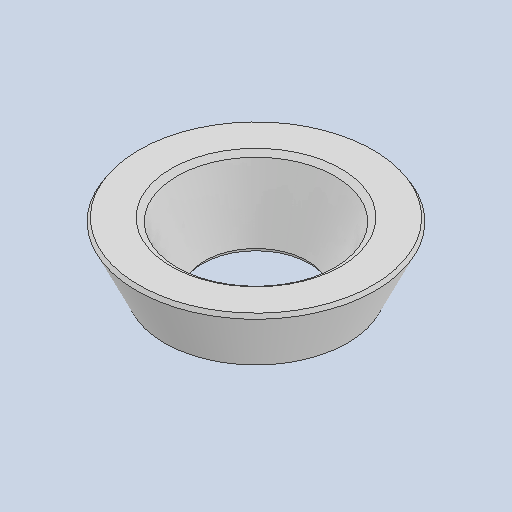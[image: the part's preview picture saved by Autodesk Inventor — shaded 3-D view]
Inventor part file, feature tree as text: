
AUTODESK INVENTOR PART (.ipt)
format: ipt  version: 2023 (Build 270158000, 158)  size: 247,808 bytes
history: native  units: mm
features: revolve x1, chamfer x1, sketch x1
ambient origin geometry x8: Origin, YZ Plane, XZ Plane, XY Plane, X Axis, Y Axis, Z Axis, Center Point
bodies: Solid1 (feature_tree)
feature tree (3):
  revolve  "Revolution1"  [1 undecoded]
  chamfer  "Chamfer1"  Distance=8.0mm
  sketch  "Sketch1"  dims[d1=3.3mm d3=2.0mm d5=8.0mm d6=4.9mm d7=90.0deg d8=0.2mm d9=2.0mm d10=45.0deg]
note: 1 required parameter value undecoded (feature->parameter linkage not recoverable at this tier; creation-order binding heuristic only, values carry confidence <= 0.55)
